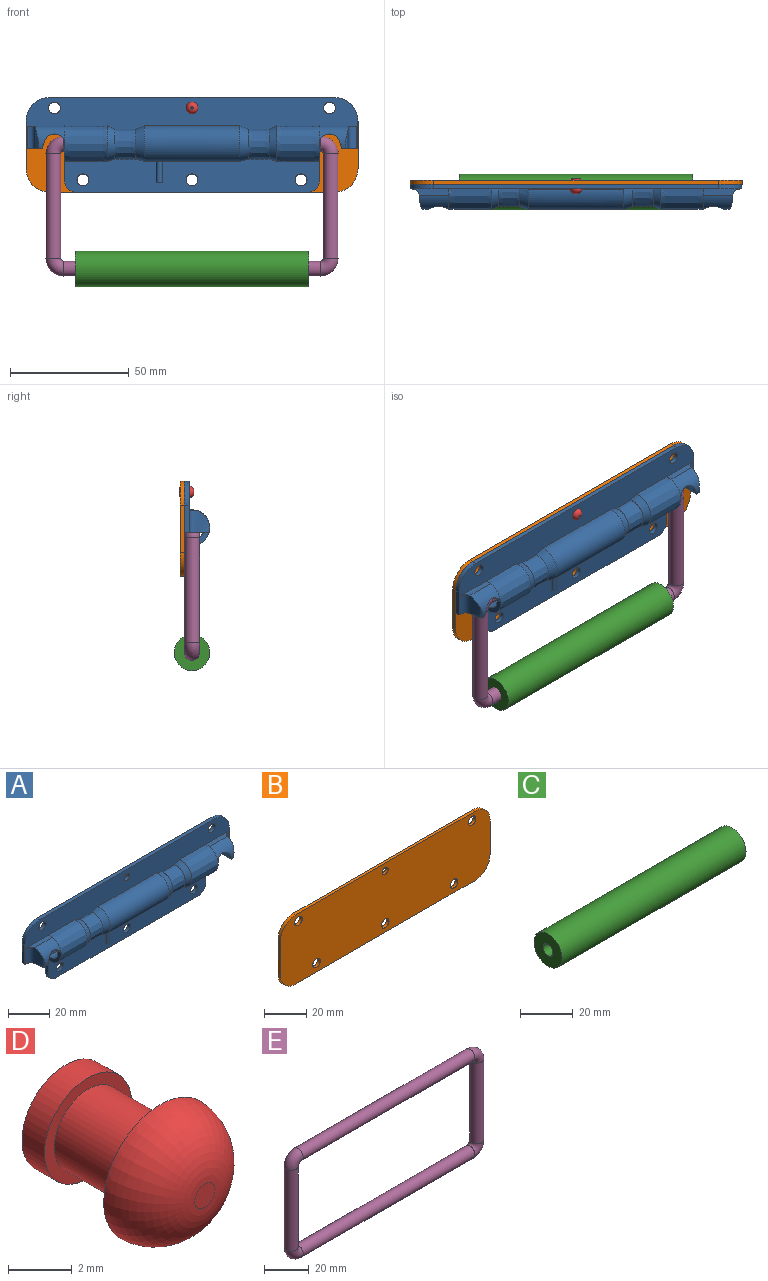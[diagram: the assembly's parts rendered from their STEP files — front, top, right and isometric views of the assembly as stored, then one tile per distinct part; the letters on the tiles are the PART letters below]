
ASSEMBLY  parts=5 mates=4
PART A: 71 faces, bbox 140x11.2x40 mm
  f0: plane 16.43x2mm, normal (-1,0,0), area 32.8mm2, adj f1,f8,f9,f15,f17,f33,f34
  f1: plane 140.05x40.05mm, normal (0,-1,0), area 4288.7mm2, adj f0,f2,f3,f4,f5,f6,f7,f8
  f2: plane 11.51x2mm, normal (1,0,0), area 23mm2, adj f1,f3,f14,f15
  f3: cylinder r=10mm len=10mm, axis (0,-1,0), area 31.4mm2, adj f1,f2,f4,f15
  f4: plane 120x2mm, normal (0,0,1), area 240mm2, adj f1,f3,f5,f15
  f5: cylinder r=10mm len=10mm, axis (0,-1,0), area 31.4mm2, adj f1,f4,f6,f15
  f6: plane 11.51x2mm, normal (-1,0,0), area 23mm2, adj f1,f5,f7,f15
  f7: plane 11.19x6.87mm, normal (0,0,-1), area 38.5mm2, adj f1,f6,f8,f15,f59,f61
  f8: extruded ~10.63x9.36mm, area 144.9mm2, adj f0,f1,f7,f15,f34,f35,f36,f58
  f9: cylinder r=5mm len=5mm, axis (0,-1,0), area 15.7mm2, adj f0,f1,f10,f15
  f10: plane 97.55x2mm, normal (0,0,-1), area 195.1mm2, adj f1,f9,f11,f15
  f11: cylinder r=5mm len=5mm, axis (0,-1,0), area 15.7mm2, adj f1,f10,f12,f15
  f12: plane 16.43x2mm, normal (1,0,0), area 32.8mm2, adj f1,f11,f13,f15,f16,f18,f39
  f13: extruded ~10.63x9.36mm, area 144.9mm2, adj f1,f12,f14,f15,f39,f40,f53,f54
  f14: plane 11.19x6.87mm, normal (0,0,-1), area 38.5mm2, adj f1,f2,f13,f15,f55,f57
  f15: plane 140x40mm, normal (0,1,0), area 4742.4mm2, adj f0,f2,f3,f4,f5,f6,f7,f8
  f16: plane 2.23x0.02mm, normal (0,1,0), area 0mm2, adj f12,f18,f39,f50
  f17: extruded ~0.02x0.01mm, area 0mm2, adj f0,f20,f33,f38
  f18: extruded ~0.02x0.01mm, area 0mm2, adj f12,f16,f50,f52
  f19: plane 2.6x0.15mm, normal (-1,0,0), area 0.3mm2, adj f1,f34,f60
  f20: plane 2.6x2.33mm, normal (-1,0,0), area 0.3mm2, adj f17,f33,f34,f37,f38
  f21: plane 40.21x2.23mm, normal (0,1,-0.01), area 89.8mm2, adj f22,f24,f27,f44,f68,f69
  f22: cylinder r=7.47mm len=40.21mm, axis (-1,0,0), area 1034.9mm2, adj f21,f23,f26,f43,f69
  f23: plane 40.21x2.23mm, normal (0,1,0), area 89.8mm2, adj f22,f24,f25,f42
  f24: cylinder r=5.28mm len=40.21mm, axis (-1,0,0), area 761.6mm2, adj f21,f23,f28,f45
  f25: bspline ~2.72x2.46mm, area 4.9mm2, adj f1,f23,f26,f28
  f26: bspline ~14.95x8.69mm, area 95.4mm2, adj f1,f22,f25,f27,f29
  f27: bspline ~2.78x2.23mm, area 4.9mm2, adj f1,f21,f26,f28
  f28: bspline ~10.67x6.49mm, area 71.2mm2, adj f1,f24,f25,f27,f30
  f29: extruded ~12.61x8.6mm, area 189.6mm2, adj f1,f26,f32
  f30: extruded ~10.36x8.6mm, area 159.2mm2, adj f1,f28,f31
  f31: bspline ~10.67x6.45mm, area 61.9mm2, adj f1,f30,f35
  f32: bspline ~14.95x8.64mm, area 84mm2, adj f1,f29,f34
  f33: plane 2.23x0.02mm, normal (0,1,0), area 0mm2, adj f0,f17,f20,f34
  f34: extruded ~17.99x14.93mm, area 463.9mm2, adj f0,f1,f8,f19,f20,f32,f33,f36
  f35: extruded ~17.99x10.56mm, area 340.1mm2, adj f1,f8,f31,f36,f58
  f36: plane 8.63x8.22mm, normal (-1,0,0), area 26.2mm2, adj f8,f34,f35,f37,f38
  f37: extruded ~2.8x0.05mm, area 0.1mm2, adj f20,f34,f36,f38
  f38: plane 2.18x0.02mm, normal (0,-1,0), area 0mm2, adj f17,f20,f36,f37
  f39: extruded ~17.99x14.93mm, area 463.9mm2, adj f1,f12,f13,f16,f41,f49,f50,f51
  f40: extruded ~17.99x10.56mm, area 340.1mm2, adj f1,f13,f48,f53,f54
  f41: plane 2.6x0.15mm, normal (1,0,0), area 0.3mm2, adj f1,f39,f56
  f42: bspline ~2.72x2.46mm, area 4.9mm2, adj f1,f23,f43,f45
  f43: bspline ~15.1x8.69mm, area 95.4mm2, adj f1,f22,f42,f44,f46
  f44: bspline ~2.78x2.23mm, area 4.9mm2, adj f1,f21,f43,f45
  f45: bspline ~10.67x6.49mm, area 71.2mm2, adj f1,f24,f42,f44,f47
  f46: extruded ~12.61x8.6mm, area 189.6mm2, adj f1,f43,f49
  f47: extruded ~10.36x8.6mm, area 159.2mm2, adj f1,f45,f48
  f48: bspline ~10.67x6.45mm, area 61.9mm2, adj f1,f40,f47
  f49: bspline ~14.95x8.64mm, area 84mm2, adj f1,f39,f46
  f50: plane 2.6x2.33mm, normal (1,0,0), area 0.3mm2, adj f16,f18,f39,f51,f52
  f51: extruded ~2.8x0.05mm, area 0.1mm2, adj f39,f50,f52,f53
  f52: plane 2.18x0.02mm, normal (0,-1,0), area 0mm2, adj f18,f50,f51,f53
  f53: plane 8.63x8.22mm, normal (1,0,0), area 26.2mm2, adj f13,f39,f40,f51,f52
  f54: plane 6.33x4.24mm, normal (-1,0,0), area 21.2mm2, adj f1,f13,f40
  f55: extruded ~9.35x8.63mm, area 91.1mm2, adj f1,f14,f56,f57
  f56: plane 15.78x2.8mm, normal (0,0,1), area 33.9mm2, adj f1,f41,f55,f57
  f57: cylinder r=7.47mm len=12.32mm, axis (-1,0,0), area 96.3mm2, adj f13,f14,f39,f55,f56
  f58: plane 6.33x4.24mm, normal (1,0,0), area 21.2mm2, adj f1,f8,f35
  f59: extruded ~9.35x8.63mm, area 91.1mm2, adj f1,f7,f60,f61
  f60: plane 15.79x2.8mm, normal (0,0,1), area 33.9mm2, adj f1,f19,f59,f61
  f61: cylinder r=7.47mm len=12.32mm, axis (1,0,0), area 96.3mm2, adj f7,f8,f34,f59,f60
  f62: cylinder r=2.5mm len=5mm, axis (0,-1,0), area 31.4mm2, adj f1,f15
  f63: cylinder r=2.5mm len=5mm, axis (0,-1,0), area 31.4mm2, adj f1,f15
  f64: cylinder r=2.5mm len=5mm, axis (0,-1,0), area 31.4mm2, adj f1,f15
  f65: cylinder r=2.5mm len=5mm, axis (0,-1,0), area 31.4mm2, adj f1,f15
  f66: cylinder r=2.5mm len=5mm, axis (0,-1,0), area 31.4mm2, adj f1,f15
  f67: plane 2.55x1.27mm, normal (0,0,-1), area 2.6mm2, adj f1,f69
  f68: plane 2.55x0.05mm, normal (0,0,1), area 0.1mm2, adj f1,f21,f69
  f69: cylinder r=1.27mm len=9.1mm, axis (0,0,1), area 36.1mm2, adj f1,f21,f22,f67,f68
  f70: cylinder r=2mm len=4mm, axis (0,-1,0), area 25.1mm2, adj f1,f15
PART B: 16 faces, bbox 140x1.7x40 mm
  f0: plane 120x1.7mm, normal (0,0,-1), area 204mm2, adj f1,f7,f8,f9
  f1: cylinder r=10mm len=10mm, axis (0,-1,0), area 26.7mm2, adj f0,f2,f8,f9
  f2: plane 20x1.7mm, normal (-1,0,0), area 34mm2, adj f1,f3,f8,f9
  f3: cylinder r=10mm len=10mm, axis (0,-1,0), area 26.7mm2, adj f2,f4,f8,f9
  f4: plane 120x1.7mm, normal (0,0,1), area 204mm2, adj f3,f5,f8,f9
  f5: cylinder r=10mm len=10mm, axis (0,-1,0), area 26.7mm2, adj f4,f6,f8,f9
  f6: plane 20x1.7mm, normal (1,0,0), area 34mm2, adj f5,f7,f8,f9
  f7: cylinder r=10mm len=10mm, axis (0,-1,0), area 26.7mm2, adj f0,f6,f8,f9
  f8: plane 140x40mm, normal (0,1,0), area 5403.4mm2, adj f0,f1,f2,f3,f4,f5,f6,f7
  f9: plane 140x40mm, normal (0,-1,0), area 5403.4mm2, adj f0,f1,f2,f3,f4,f5,f6,f7
  f10: cylinder r=2.5mm len=5mm, axis (0,-1,0), area 26.7mm2, adj f8,f9
  f11: cylinder r=2.5mm len=5mm, axis (0,-1,0), area 26.7mm2, adj f8,f9
  f12: cylinder r=2.5mm len=5mm, axis (0,-1,0), area 26.7mm2, adj f8,f9
  f13: cylinder r=2.5mm len=5mm, axis (0,-1,0), area 26.7mm2, adj f8,f9
  f14: cylinder r=2.5mm len=5mm, axis (0,-1,0), area 26.7mm2, adj f8,f9
  f15: cylinder r=2mm len=4mm, axis (0,-1,0), area 21.4mm2, adj f8,f9
PART C: 4 faces, bbox 98.4x15x15 mm
  f0: cylinder r=2.61mm len=98.4mm, axis (-1,0,0), area 1611.8mm2, adj f2,f3
  f1: cylinder r=7.5mm len=98.4mm, axis (-1,0,0), area 4637mm2, adj f2,f3
  f2: plane 15x15mm, normal (1,0,0), area 155.4mm2, adj f0,f1
  f3: plane 15x15mm, normal (-1,0,0), area 155.4mm2, adj f0,f1
PART D: 7 faces, bbox 5x6.2x5 mm
  f0: cylinder r=1.5mm len=3.2mm, axis (0,-1,0), area 30.2mm2, adj f2,f5
  f1: plane 0.9x0.9mm, normal (0,-1,0), area 0.6mm2, adj f3
  f2: plane 5x5mm, normal (0,1,0), area 12.6mm2, adj f0,f3
  f3: torus R=0.45mm, axis (0,1,0), area 34.7mm2, adj f1,f2
  f4: cylinder r=1.94mm len=3.88mm, axis (0,1,0), area 12.2mm2, adj f5,f6
  f5: plane 3.88x3.88mm, normal (0,-1,0), area 4.7mm2, adj f0,f4
  f6: plane 3.88x3.88mm, normal (0,1,0), area 11.8mm2, adj f4
PART E: 8 faces, bbox 124.5x6.4x60.4 mm
  f0: torus R=4.32mm, axis (0,1,0), area 135.2mm2, adj f1,f7
  f1: cylinder r=3.17mm len=44.16mm, axis (0,0,1), area 881mm2, adj f0,f2
  f2: torus R=4.32mm, axis (0,1,0), area 135.2mm2, adj f1,f3
  f3: cylinder r=3.17mm len=108.33mm, axis (-1,0,0), area 2161mm2, adj f2,f4
  f4: torus R=4.32mm, axis (0,1,0), area 135.2mm2, adj f3,f5
  f5: cylinder r=3.17mm len=44.16mm, axis (0,0,-1), area 881mm2, adj f4,f6
  f6: torus R=4.32mm, axis (0,1,0), area 135.2mm2, adj f5,f7
  f7: cylinder r=3.17mm len=108.33mm, axis (1,0,0), area 2161mm2, adj f0,f6
PLACE A t=(-142.3,13.87,11)mm fixed
PLACE B t=(-142.3,13.87,11)mm
PLACE C rot(axis=(0,0,-1),180deg) t=(-142.26,9.77,11.45)mm
PLACE D t=(-142.3,13.87,38.11)mm
PLACE E rot(axis=(0,0,-1),180deg) t=(-142.3,9.5,11.49)mm
MATE fastened C.f0 <-> E.f3  axis (-1,0,0) through (-191.46,12.67,-29.72)mm
MATE revolute A.f22 <-> E.f7  axis (-1,0,0) through (-142.3,12.67,23.07)mm
MATE fastened A.f65 <-> B.f13  axis (0,1,0) through (-96.3,15.87,7.77)mm
MATE fastened D.f3 <-> A.f70  axis (0,1,0) through (-142.3,13.87,38.11)mm
